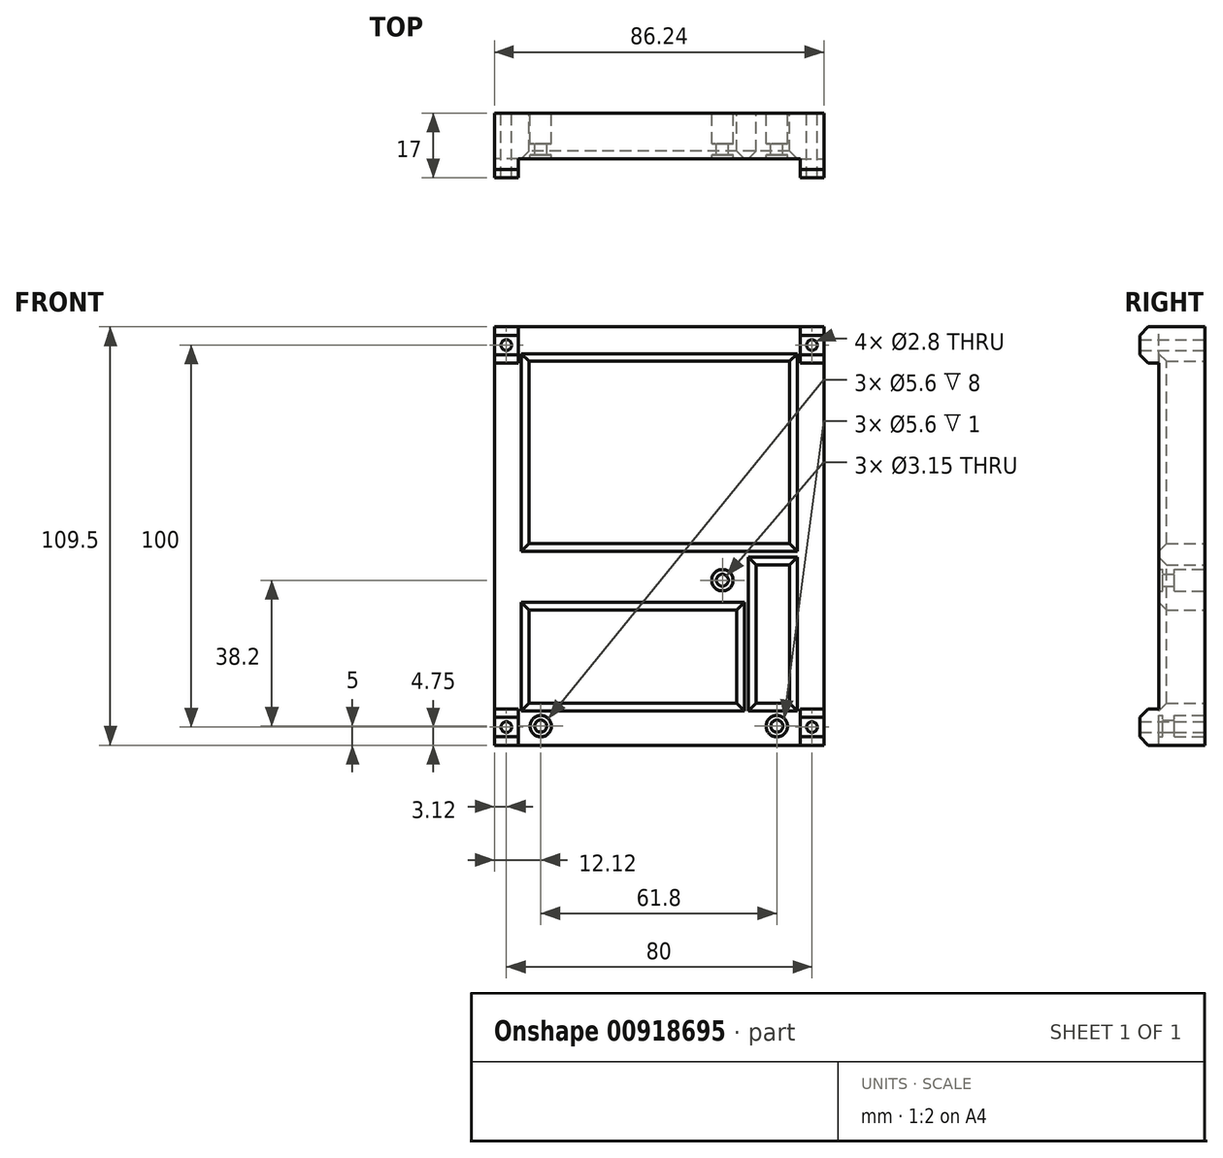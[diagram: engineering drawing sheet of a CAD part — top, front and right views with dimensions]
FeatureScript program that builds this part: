
annotation { "Feature Type Name" : "Feature", "Feature Type Description" : "" }
export const myFeature = defineFeature(function(context is Context, id is Id, definition is map)
    precondition{}
    {
        {
            var Q0;
            Q0=qCreatedBy(makeId("Front.planeOp"),FACE);
            var sketch = newSketch(context, id + "F0", { "sketchPlane" : qUnion([Q0])});
            skPoint(sketch, "E0.middle", {"position": v(0, 0) * mm});
            skCircle(sketch, "E1", {"center": v(-40, 50) * mm, "radius": 1.4 * mm});
            skCircle(sketch, "E2", {"center": v(40, 50) * mm, "radius": 1.4 * mm});
            skCircle(sketch, "E3", {"center": v(-40, -50) * mm, "radius": 1.4 * mm});
            skCircle(sketch, "E4", {"center": v(40, -50) * mm, "radius": 1.4 * mm});
            skLineSegment(sketch, "E5.bottom", {"start": v(43.12, -54.75) * mm, "end": v(-43.12, -54.75) * mm});
            skLineSegment(sketch, "E5.top", {"start": v(43.12, 54.75) * mm, "end": v(-43.12, 54.75) * mm});
            skLineSegment(sketch, "E5.left", {"start": v(43.12, -54.75) * mm, "end": v(43.12, 54.75) * mm});
            skLineSegment(sketch, "E5.right", {"start": v(-43.12, -54.75) * mm, "end": v(-43.12, 54.75) * mm});
            skLineSegment(sketch, "E6.bottom", {"start": v(-36.88, -54.75) * mm, "end": v(-43.13, -54.75) * mm});
            skLineSegment(sketch, "E6.top", {"start": v(-36.88, -45.25) * mm, "end": v(-43.13, -45.25) * mm});
            skLineSegment(sketch, "E6.left", {"start": v(-36.88, -54.75) * mm, "end": v(-36.88, -45.25) * mm});
            skLineSegment(sketch, "E6.right", {"start": v(-43.13, -54.75) * mm, "end": v(-43.13, -45.25) * mm});
            skLineSegment(sketch, "E7.bottom", {"start": v(36.88, -54.75) * mm, "end": v(43.12, -54.75) * mm});
            skLineSegment(sketch, "E7.top", {"start": v(36.88, -45.25) * mm, "end": v(43.12, -45.25) * mm});
            skLineSegment(sketch, "E7.left", {"start": v(36.88, -54.75) * mm, "end": v(36.88, -45.25) * mm});
            skLineSegment(sketch, "E7.right", {"start": v(43.12, -54.75) * mm, "end": v(43.12, -45.25) * mm});
            skLineSegment(sketch, "E8.bottom", {"start": v(-36.88, 45.25) * mm, "end": v(-43.13, 45.25) * mm});
            skLineSegment(sketch, "E8.top", {"start": v(-36.88, 54.75) * mm, "end": v(-43.13, 54.75) * mm});
            skLineSegment(sketch, "E8.left", {"start": v(-36.88, 45.25) * mm, "end": v(-36.88, 54.75) * mm});
            skLineSegment(sketch, "E8.right", {"start": v(-43.13, 45.25) * mm, "end": v(-43.13, 54.75) * mm});
            skLineSegment(sketch, "E9.bottom", {"start": v(36.88, 45.25) * mm, "end": v(43.12, 45.25) * mm});
            skLineSegment(sketch, "E9.top", {"start": v(36.87, 54.75) * mm, "end": v(43.12, 54.75) * mm});
            skLineSegment(sketch, "E9.left", {"start": v(36.88, 45.25) * mm, "end": v(36.88, 54.75) * mm});
            skLineSegment(sketch, "E9.right", {"start": v(43.12, 45.25) * mm, "end": v(43.12, 54.75) * mm});
            skCircle(sketch, "E10.cCircle", {"center": v(40, 50) * mm, "radius": 3.08 * mm, "construction": true});
            skLineSegment(sketch, "E10.0", {"start": v(36.92, 48.22) * mm, "end": v(36.92, 51.78) * mm});
            skLineSegment(sketch, "E10.1", {"start": v(36.93, 51.78) * mm, "end": v(40, 53.55) * mm});
            skLineSegment(sketch, "E10.2", {"start": v(40, 53.55) * mm, "end": v(43.07, 51.78) * mm});
            skLineSegment(sketch, "E10.3", {"start": v(43.07, 51.78) * mm, "end": v(43.08, 48.22) * mm});
            skLineSegment(sketch, "E10.4", {"start": v(43.08, 48.22) * mm, "end": v(40, 46.45) * mm});
            skLineSegment(sketch, "E10.5", {"start": v(40, 46.45) * mm, "end": v(36.93, 48.22) * mm});
            skPoint(sketch, "E10.0.midPoint", {"position": v(36.92, 50) * mm});
            skCircle(sketch, "E11.cCircle", {"center": v(-40, 50) * mm, "radius": 3.08 * mm, "construction": true});
            skLineSegment(sketch, "E11.0", {"start": v(-36.92, 51.78) * mm, "end": v(-36.92, 48.22) * mm});
            skLineSegment(sketch, "E11.1", {"start": v(-36.92, 48.22) * mm, "end": v(-40, 46.45) * mm});
            skLineSegment(sketch, "E11.2", {"start": v(-40, 46.45) * mm, "end": v(-43.07, 48.22) * mm});
            skLineSegment(sketch, "E11.3", {"start": v(-43.07, 48.22) * mm, "end": v(-43.07, 51.78) * mm});
            skLineSegment(sketch, "E11.4", {"start": v(-43.08, 51.78) * mm, "end": v(-40, 53.55) * mm});
            skLineSegment(sketch, "E11.5", {"start": v(-40, 53.55) * mm, "end": v(-36.92, 51.78) * mm});
            skPoint(sketch, "E11.0.midPoint", {"position": v(-36.92, 50) * mm});
            skCircle(sketch, "E12.cCircle", {"center": v(40, -50) * mm, "radius": 3.08 * mm, "construction": true});
            skPoint(sketch, "E12.cCircle.perimeterSnap0", {"position": v(43.12, -50) * mm});
            skLineSegment(sketch, "E12.0", {"start": v(43.08, -48.22) * mm, "end": v(43.08, -51.78) * mm});
            skLineSegment(sketch, "E12.1", {"start": v(43.07, -51.78) * mm, "end": v(40, -53.55) * mm});
            skLineSegment(sketch, "E12.2", {"start": v(40, -53.55) * mm, "end": v(36.93, -51.78) * mm});
            skLineSegment(sketch, "E12.3", {"start": v(36.93, -51.78) * mm, "end": v(36.93, -48.22) * mm});
            skLineSegment(sketch, "E12.4", {"start": v(36.93, -48.22) * mm, "end": v(40, -46.45) * mm});
            skLineSegment(sketch, "E12.5", {"start": v(40, -46.45) * mm, "end": v(43.07, -48.22) * mm});
            skPoint(sketch, "E12.0.midPoint", {"position": v(43.08, -50) * mm});
            skPoint(sketch, "E12.0.midPoint.positionSnap0", {"position": v(43.12, -50) * mm});
            skCircle(sketch, "E13.cCircle", {"center": v(-40, -50) * mm, "radius": 3.08 * mm, "construction": true});
            skLineSegment(sketch, "E13.0", {"start": v(-36.93, -48.22) * mm, "end": v(-36.93, -51.78) * mm});
            skLineSegment(sketch, "E13.1", {"start": v(-36.93, -51.78) * mm, "end": v(-40, -53.55) * mm});
            skLineSegment(sketch, "E13.2", {"start": v(-40, -53.55) * mm, "end": v(-43.08, -51.78) * mm});
            skLineSegment(sketch, "E13.3", {"start": v(-43.08, -51.78) * mm, "end": v(-43.08, -48.22) * mm});
            skLineSegment(sketch, "E13.4", {"start": v(-43.08, -48.22) * mm, "end": v(-40, -46.45) * mm});
            skLineSegment(sketch, "E13.5", {"start": v(-40, -46.45) * mm, "end": v(-36.93, -48.22) * mm});
            skPoint(sketch, "E13.0.midPoint", {"position": v(-36.93, -50) * mm});
            skCircle(sketch, "E14", {"center": v(-31, -49.75) * mm, "radius": 1.57 * mm});
            skCircle(sketch, "E15", {"center": v(30.8, -49.75) * mm, "radius": 1.57 * mm});
            skCircle(sketch, "E16", {"center": v(-31, -49.75) * mm, "radius": 2.8 * mm});
            skCircle(sketch, "E17", {"center": v(30.8, -49.75) * mm, "radius": 2.8 * mm});
            skCircle(sketch, "E18", {"center": v(16.55, -11.55) * mm, "radius": 2.8 * mm});
            skCircle(sketch, "E19", {"center": v(16.55, -11.55) * mm, "radius": 1.57 * mm});
            skLineSegment(sketch, "E20", {"start": v(-31, -49.75) * mm, "end": v(30.8, -49.75) * mm, "construction": true});
            skLineSegment(sketch, "E21", {"start": v(16.55, -11.55) * mm, "end": v(16.55, -49.75) * mm, "construction": true});
            skSolve(sketch);
        }
        {
            var Q0;
            {var subQ3=sQuery(id+"F0.wireOp",EDGE,"E6.top");Q0=makeQuery(id+"F0.imprint","IMPRINT",FACE,{"disambiguationData":[TD([[makeQuery(id+"F0.imprint","IMPRINT",EDGE,{"derivedFrom":subQ3}),-1.0]])]});}
            var Q1;
            {var subQ0=sQuery(id+"F0.wireOp",EDGE,"LAEbAKdu-djDs-V827-S9WD-6yGzL6sm2GWT");Q1=makeQuery(id+"F0.imprint","IMPRINT",FACE,{"disambiguationData":[TD([[makeQuery(id+"F0.imprint","IMPRINT",EDGE,{"derivedFrom":subQ0}),1.0]])]});}
            var Q2;
            Q2=makeQuery(id+"F0.imprint","IMPRINT",FACE,{"disambiguationData":[TD([[makeQuery(id+"F0.imprint","IMPRINT",EDGE,{"derivedFrom":sQuery(id+"F0.wireOp",EDGE,"344f14d0-57c9-4bf9-bac3-c7a6806c6285.bottom")}),-1.0]])]});
            var Q3;
            Q3=makeQuery(id+"F0.imprint","IMPRINT",FACE,{"disambiguationData":[TD([[makeQuery(id+"F0.imprint","IMPRINT",EDGE,{"derivedFrom":sQuery(id+"F0.wireOp",EDGE,"9oMv4eh1-cItz-VmmB-YfER-I7rwddDMCMIy.bottom")}),-1.0]])]});
            var Q4;
            Q4=makeQuery(id+"F0.imprint","IMPRINT",FACE,{"disambiguationData":[TD([[makeQuery(id+"F0.imprint","IMPRINT",EDGE,{"derivedFrom":sQuery(id+"F0.wireOp",EDGE,"1293f738-cd9c-4ca6-888c-53c8c5076d64.bottom")}),-1.0]])]});
            var Q5;
            Q5=makeQuery(id+"F0.imprint","IMPRINT",FACE,{"disambiguationData":[TD([[makeQuery(id+"F0.imprint","IMPRINT",EDGE,{"derivedFrom":sQuery(id+"F0.wireOp",EDGE,"8f083a88-c7b4-469a-ac29-3101791f455f.bottom")}),-1.0]])]});
            var Q6;
            Q6=makeQuery(id+"F0.imprint","IMPRINT",FACE,{"disambiguationData":[TD([[makeQuery(id+"F0.imprint","IMPRINT",EDGE,{"derivedFrom":sQuery(id+"F0.wireOp",EDGE,"92fa807a-3ddb-4387-94e5-abf9c8788f89.bottom")}),-1.0]])]});
            var Q7;
            Q7=makeQuery(id+"F0.imprint","IMPRINT",FACE,{"disambiguationData":[TD([[makeQuery(id+"F0.imprint","IMPRINT",EDGE,{"derivedFrom":sQuery(id+"F0.wireOp",EDGE,"303d7d46-c817-43ee-aa70-cb5fa533f4f4.bottom")}),-1.0]])]});
            extrude(context, id + "F1", {"entities" : qUnion([Q0, Q1, Q2, Q3, Q4, Q5, Q6, Q7]), "depth" : 12 * mm, "offsetDistance" : 25 * mm});
        }
        {
            var Q0;
            Q0=makeQuery(id+"F0.imprint","IMPRINT",FACE,{"disambiguationData":[TD([[makeQuery(id+"F0.imprint","IMPRINT",EDGE,{"derivedFrom":sQuery(id+"F0.wireOp",EDGE,"E3")}),-1.0]])]});
            var Q1;
            Q1=makeQuery(id+"F0.imprint","IMPRINT",FACE,{"disambiguationData":[TD([[makeQuery(id+"F0.imprint","IMPRINT",EDGE,{"derivedFrom":sQuery(id+"F0.wireOp",EDGE,"E4")}),-1.0]])]});
            var Q2;
            Q2=makeQuery(id+"F0.imprint","IMPRINT",FACE,{"disambiguationData":[TD([[makeQuery(id+"F0.imprint","IMPRINT",EDGE,{"derivedFrom":sQuery(id+"F0.wireOp",EDGE,"E2")}),-1.0]])]});
            var Q3;
            Q3=makeQuery(id+"F0.imprint","IMPRINT",FACE,{"disambiguationData":[TD([[makeQuery(id+"F0.imprint","IMPRINT",EDGE,{"derivedFrom":sQuery(id+"F0.wireOp",EDGE,"E1")}),-1.0]])]});
            var Q4;
            {var subQ1=sQuery(id+"F0.wireOp",EDGE,"E7.top");Q4=makeQuery(id+"F0.imprint","IMPRINT",FACE,{"disambiguationData":[TD([[makeQuery(id+"F0.imprint","IMPRINT",EDGE,{"derivedFrom":subQ1}),-1.0]])]});}
            var Q5;
            {var subQ1=sQuery(id+"F0.wireOp",EDGE,"E6.top");Q5=makeQuery(id+"F0.imprint","IMPRINT",FACE,{"disambiguationData":[TD([[makeQuery(id+"F0.imprint","IMPRINT",EDGE,{"derivedFrom":subQ1}),1.0]])]});}
            var Q6;
            {var subQ1=sQuery(id+"F0.wireOp",EDGE,"E8.bottom");Q6=makeQuery(id+"F0.imprint","IMPRINT",FACE,{"disambiguationData":[TD([[makeQuery(id+"F0.imprint","IMPRINT",EDGE,{"derivedFrom":subQ1}),-1.0]])]});}
            var Q7;
            {var subQ0=sQuery(id+"F0.wireOp",EDGE,"E9.bottom");Q7=makeQuery(id+"F0.imprint","IMPRINT",FACE,{"disambiguationData":[TD([[makeQuery(id+"F0.imprint","IMPRINT",EDGE,{"derivedFrom":subQ0}),1.0]])]});}
            extrude(context, id + "F2", {"entities" : qUnion([Q0, Q1, Q2, Q3, Q4, Q5, Q6, Q7]), "operationType" : NewBodyOperationType.ADD, "depth" : 17 * mm, "offsetDistance" : 25 * mm});
        }
        {
            var Q0;
            Q0=makeQuery(id+"F2.opExtrude","CAP_EDGE",EDGE,{"disambiguationData":[OSD([sQuery(id+"F0.wireOp",EDGE,"E6.top")])],"isStart":false});
            var Q1;
            {var subQ0=sQuery(id+"F0.wireOp",EDGE,"E5.bottom");Q1=makeQuery(id+"F2.opExtrude","CAP_EDGE",EDGE,{"disambiguationData":[OSD([subQ0]),TDD([makeQuery(id+"F0.imprint","IMPRINT",EDGE,{"disambiguationData":[TD([[makeQuery(id+"F0.imprint","INTERSECT",VERTEX,{"derivedFrom":[subQ0,sQuery(id+"F0.wireOp",EDGE,"E6.left")]}),-1.0]])],"derivedFrom":subQ0})])],"isStart":false});}
            var Q2;
            Q2=makeQuery(id+"F2.opExtrude","CAP_EDGE",EDGE,{"disambiguationData":[OSD([sQuery(id+"F0.wireOp",EDGE,"E7.top")])],"isStart":false});
            var Q3;
            {var subQ0=sQuery(id+"F0.wireOp",EDGE,"E5.bottom");Q3=makeQuery(id+"F2.opExtrude","CAP_EDGE",EDGE,{"disambiguationData":[OSD([subQ0]),TDD([makeQuery(id+"F0.imprint","IMPRINT",EDGE,{"disambiguationData":[TD([[makeQuery(id+"F0.imprint","INTERSECT",VERTEX,{"derivedFrom":[subQ0,sQuery(id+"F0.wireOp",EDGE,"E7.left")]}),1.0]])],"derivedFrom":subQ0})])],"isStart":false});}
            var Q4;
            {var subQ0=sQuery(id+"F0.wireOp",EDGE,"E5.top");Q4=makeQuery(id+"F2.opExtrude","CAP_EDGE",EDGE,{"disambiguationData":[OSD([subQ0]),TDD([makeQuery(id+"F0.imprint","IMPRINT",EDGE,{"disambiguationData":[TD([[makeQuery(id+"F0.imprint","INTERSECT",VERTEX,{"derivedFrom":[subQ0,sQuery(id+"F0.wireOp",EDGE,"E5.right")]}),1.0]])],"derivedFrom":subQ0})])],"isStart":false});}
            var Q5;
            Q5=makeQuery(id+"F2.opExtrude","CAP_EDGE",EDGE,{"disambiguationData":[OSD([sQuery(id+"F0.wireOp",EDGE,"E8.bottom")])],"isStart":false});
            var Q6;
            {var subQ0=sQuery(id+"F0.wireOp",EDGE,"E5.top");Q6=makeQuery(id+"F2.opExtrude","CAP_EDGE",EDGE,{"disambiguationData":[OSD([subQ0]),TDD([makeQuery(id+"F0.imprint","IMPRINT",EDGE,{"disambiguationData":[TD([[makeQuery(id+"F0.imprint","INTERSECT",VERTEX,{"derivedFrom":[subQ0,sQuery(id+"F0.wireOp",EDGE,"E9.left")]}),1.0]])],"derivedFrom":subQ0})])],"isStart":false});}
            var Q7;
            Q7=makeQuery(id+"F2.opExtrude","CAP_EDGE",EDGE,{"disambiguationData":[OSD([sQuery(id+"F0.wireOp",EDGE,"E9.bottom")])],"isStart":false});
            chamfer(context, id + "F3", {"entities" : qUnion([Q0, Q1, Q2, Q3, Q4, Q5, Q6, Q7]), "width" : 2.2 * mm, "tangentPropagation" : true});
        }
        {
            var Q0;
            Q0=makeQuery(id+"F0.imprint","IMPRINT",FACE,{"disambiguationData":[TD([[makeQuery(id+"F0.imprint","IMPRINT",EDGE,{"derivedFrom":sQuery(id+"F0.wireOp",EDGE,"E18")}),1.0]])]});
            var Q1;
            Q1=makeQuery(id+"F0.imprint","IMPRINT",FACE,{"disambiguationData":[TD([[makeQuery(id+"F0.imprint","IMPRINT",EDGE,{"derivedFrom":sQuery(id+"F0.wireOp",EDGE,"E15")}),-1.0]])]});
            var Q2;
            Q2=makeQuery(id+"F0.imprint","IMPRINT",FACE,{"disambiguationData":[TD([[makeQuery(id+"F0.imprint","IMPRINT",EDGE,{"derivedFrom":sQuery(id+"F0.wireOp",EDGE,"E14")}),-1.0]])]});
            extrude(context, id + "F4", {"entities" : qUnion([Q0, Q1, Q2]), "operationType" : NewBodyOperationType.ADD, "depth" : 11 * mm, "offsetDistance" : 25 * mm, "hasSecondDirection" : true, "secondDirectionOppositeDirection" : true, "secondDirectionDepth" : -8 * mm});
        }
        {
            var Q0;
            {var subQ0=sQuery(id+"F0.wireOp",EDGE,"E7.left");var subQ1=sQuery(id+"F0.wireOp",EDGE,"E7.top");var subQ2=sQuery(id+"F0.wireOp",EDGE,"E5.left");var subQ3=sQuery(id+"F0.wireOp",EDGE,"E5.bottom");var subQ4=sQuery(id+"F0.wireOp",EDGE,"E6.left");var subQ5=sQuery(id+"F0.wireOp",EDGE,"E6.top");var subQ6=sQuery(id+"F0.wireOp",EDGE,"E5.right");var subQ7=sQuery(id+"F0.wireOp",EDGE,"E9.left");var subQ8=sQuery(id+"F0.wireOp",EDGE,"E9.bottom");var subQ9=sQuery(id+"F0.wireOp",EDGE,"E5.top");var subQ10=sQuery(id+"F0.wireOp",EDGE,"E8.left");var subQ11=sQuery(id+"F0.wireOp",EDGE,"E8.bottom");Q0=makeQuery(id+"F2.boolean.opBoolean","MERGE",FACE,{"derivedFrom":[makeQuery(id+"F1.opExtrude","CAP_FACE",FACE,{"disambiguationData":[OSD([subQ3,subQ9,subQ2,subQ6,subQ5,subQ4,subQ1,subQ0,subQ11,subQ10,subQ8,subQ7,sQuery(id+"F0.wireOp",EDGE,"E16"),sQuery(id+"F0.wireOp",EDGE,"E17"),sQuery(id+"F0.wireOp",EDGE,"E18")])],"isStart":true}),makeQuery(id+"F2.opExtrude","CAP_FACE",FACE,{"disambiguationData":[OSD([sQuery(id+"F0.wireOp",EDGE,"E1"),subQ9,subQ6,subQ11,subQ10])],"isStart":true}),makeQuery(id+"F2.opExtrude","CAP_FACE",FACE,{"disambiguationData":[OSD([sQuery(id+"F0.wireOp",EDGE,"E2"),subQ9,subQ2,subQ8,subQ7])],"isStart":true}),makeQuery(id+"F2.opExtrude","CAP_FACE",FACE,{"disambiguationData":[OSD([sQuery(id+"F0.wireOp",EDGE,"E3"),subQ3,subQ6,subQ5,subQ4])],"isStart":true}),makeQuery(id+"F2.opExtrude","CAP_FACE",FACE,{"disambiguationData":[OSD([sQuery(id+"F0.wireOp",EDGE,"E4"),subQ3,subQ2,subQ1,subQ0])],"isStart":true})]});}
            var sketch = newSketch(context, id + "F5", { "sketchPlane" : qUnion([Q0])});
            skLineSegment(sketch, "E22.bottom", {"start": v(-34.12, 45.75) * mm, "end": v(34.12, 45.75) * mm});
            skLineSegment(sketch, "E22.top", {"start": v(-34.12, -2) * mm, "end": v(34.12, -2) * mm});
            skLineSegment(sketch, "E22.left", {"start": v(-34.12, 45.75) * mm, "end": v(-34.12, -2) * mm});
            skLineSegment(sketch, "E22.right", {"start": v(34.12, 45.75) * mm, "end": v(34.12, -2) * mm});
            skLineSegment(sketch, "E23.bottom", {"start": v(-34.12, -7.52) * mm, "end": v(-25.35, -7.52) * mm});
            skLineSegment(sketch, "E23.top", {"start": v(-34.12, -43.75) * mm, "end": v(-25.35, -43.75) * mm});
            skLineSegment(sketch, "E23.left", {"start": v(-34.12, -7.52) * mm, "end": v(-34.12, -43.75) * mm});
            skLineSegment(sketch, "E23.right", {"start": v(-25.35, -7.52) * mm, "end": v(-25.35, -43.75) * mm});
            skLineSegment(sketch, "E24.bottom", {"start": v(-20.35, -19.35) * mm, "end": v(34.12, -19.35) * mm});
            skLineSegment(sketch, "E24.top", {"start": v(-20.35, -43.75) * mm, "end": v(34.12, -43.75) * mm});
            skLineSegment(sketch, "E24.left", {"start": v(-20.35, -19.35) * mm, "end": v(-20.35, -43.75) * mm});
            skLineSegment(sketch, "E24.right", {"start": v(34.12, -19.35) * mm, "end": v(34.12, -43.75) * mm});
            skSolve(sketch);
        }
        {
            var Q0;
            Q0=makeQuery(id+"F5.imprint","IMPRINT",FACE,{"disambiguationData":[TD([[makeQuery(id+"F5.imprint","IMPRINT",EDGE,{"derivedFrom":sQuery(id+"F5.wireOp",EDGE,"E22.bottom")}),-1.0]])]});
            var Q1;
            Q1=makeQuery(id+"F5.imprint","IMPRINT",FACE,{"disambiguationData":[TD([[makeQuery(id+"F5.imprint","IMPRINT",EDGE,{"derivedFrom":sQuery(id+"F5.wireOp",EDGE,"E23.bottom")}),-1.0]])]});
            var Q2;
            Q2=makeQuery(id+"F5.imprint","IMPRINT",FACE,{"disambiguationData":[TD([[makeQuery(id+"F5.imprint","IMPRINT",EDGE,{"derivedFrom":sQuery(id+"F5.wireOp",EDGE,"E24.bottom")}),-1.0]])]});
            extrude(context, id + "F6", {"entities" : qUnion([Q0, Q1, Q2]), "operationType" : NewBodyOperationType.REMOVE, "oppositeDirection" : true, "depth" : 28 * mm, "offsetDistance" : 25 * mm});
        }
        {
            var Q0;
            Q0=makeQuery(id+"F6.boolean.opBoolean","INTERSECT",EDGE,{"derivedFrom":[makeQuery(id+"F1.opExtrude","CAP_FACE",FACE,{"disambiguationData":[OSD([sQuery(id+"F0.wireOp",EDGE,"E5.bottom"),sQuery(id+"F0.wireOp",EDGE,"E5.top"),sQuery(id+"F0.wireOp",EDGE,"E5.left"),sQuery(id+"F0.wireOp",EDGE,"E5.right"),sQuery(id+"F0.wireOp",EDGE,"E6.top"),sQuery(id+"F0.wireOp",EDGE,"E6.left"),sQuery(id+"F0.wireOp",EDGE,"E7.top"),sQuery(id+"F0.wireOp",EDGE,"E7.left"),sQuery(id+"F0.wireOp",EDGE,"E8.bottom"),sQuery(id+"F0.wireOp",EDGE,"E8.left"),sQuery(id+"F0.wireOp",EDGE,"E9.bottom"),sQuery(id+"F0.wireOp",EDGE,"E9.left"),sQuery(id+"F0.wireOp",EDGE,"E16"),sQuery(id+"F0.wireOp",EDGE,"E17"),sQuery(id+"F0.wireOp",EDGE,"E18")])],"isStart":false}),makeQuery(id+"F6.opExtrude","SWEPT_FACE",FACE,{"disambiguationData":[OSD([sQuery(id+"F5.wireOp",EDGE,"E22.top")])]})]});
            var Q1;
            Q1=makeQuery(id+"F6.boolean.opBoolean","INTERSECT",EDGE,{"derivedFrom":[makeQuery(id+"F1.opExtrude","CAP_FACE",FACE,{"disambiguationData":[OSD([sQuery(id+"F0.wireOp",EDGE,"E5.bottom"),sQuery(id+"F0.wireOp",EDGE,"E5.top"),sQuery(id+"F0.wireOp",EDGE,"E5.left"),sQuery(id+"F0.wireOp",EDGE,"E5.right"),sQuery(id+"F0.wireOp",EDGE,"E6.top"),sQuery(id+"F0.wireOp",EDGE,"E6.left"),sQuery(id+"F0.wireOp",EDGE,"E7.top"),sQuery(id+"F0.wireOp",EDGE,"E7.left"),sQuery(id+"F0.wireOp",EDGE,"E8.bottom"),sQuery(id+"F0.wireOp",EDGE,"E8.left"),sQuery(id+"F0.wireOp",EDGE,"E9.bottom"),sQuery(id+"F0.wireOp",EDGE,"E9.left"),sQuery(id+"F0.wireOp",EDGE,"E16"),sQuery(id+"F0.wireOp",EDGE,"E17"),sQuery(id+"F0.wireOp",EDGE,"E18")])],"isStart":false}),makeQuery(id+"F6.opExtrude","SWEPT_FACE",FACE,{"disambiguationData":[OSD([sQuery(id+"F5.wireOp",EDGE,"E22.right")])]})]});
            var Q2;
            Q2=makeQuery(id+"F6.boolean.opBoolean","INTERSECT",EDGE,{"derivedFrom":[makeQuery(id+"F1.opExtrude","CAP_FACE",FACE,{"disambiguationData":[OSD([sQuery(id+"F0.wireOp",EDGE,"E5.bottom"),sQuery(id+"F0.wireOp",EDGE,"E5.top"),sQuery(id+"F0.wireOp",EDGE,"E5.left"),sQuery(id+"F0.wireOp",EDGE,"E5.right"),sQuery(id+"F0.wireOp",EDGE,"E6.top"),sQuery(id+"F0.wireOp",EDGE,"E6.left"),sQuery(id+"F0.wireOp",EDGE,"E7.top"),sQuery(id+"F0.wireOp",EDGE,"E7.left"),sQuery(id+"F0.wireOp",EDGE,"E8.bottom"),sQuery(id+"F0.wireOp",EDGE,"E8.left"),sQuery(id+"F0.wireOp",EDGE,"E9.bottom"),sQuery(id+"F0.wireOp",EDGE,"E9.left"),sQuery(id+"F0.wireOp",EDGE,"E16"),sQuery(id+"F0.wireOp",EDGE,"E17"),sQuery(id+"F0.wireOp",EDGE,"E18")])],"isStart":false}),makeQuery(id+"F6.opExtrude","SWEPT_FACE",FACE,{"disambiguationData":[OSD([sQuery(id+"F5.wireOp",EDGE,"E22.bottom")])]})]});
            var Q3;
            Q3=makeQuery(id+"F6.boolean.opBoolean","INTERSECT",EDGE,{"derivedFrom":[makeQuery(id+"F1.opExtrude","CAP_FACE",FACE,{"disambiguationData":[OSD([sQuery(id+"F0.wireOp",EDGE,"E5.bottom"),sQuery(id+"F0.wireOp",EDGE,"E5.top"),sQuery(id+"F0.wireOp",EDGE,"E5.left"),sQuery(id+"F0.wireOp",EDGE,"E5.right"),sQuery(id+"F0.wireOp",EDGE,"E6.top"),sQuery(id+"F0.wireOp",EDGE,"E6.left"),sQuery(id+"F0.wireOp",EDGE,"E7.top"),sQuery(id+"F0.wireOp",EDGE,"E7.left"),sQuery(id+"F0.wireOp",EDGE,"E8.bottom"),sQuery(id+"F0.wireOp",EDGE,"E8.left"),sQuery(id+"F0.wireOp",EDGE,"E9.bottom"),sQuery(id+"F0.wireOp",EDGE,"E9.left"),sQuery(id+"F0.wireOp",EDGE,"E16"),sQuery(id+"F0.wireOp",EDGE,"E17"),sQuery(id+"F0.wireOp",EDGE,"E18")])],"isStart":false}),makeQuery(id+"F6.opExtrude","SWEPT_FACE",FACE,{"disambiguationData":[OSD([sQuery(id+"F5.wireOp",EDGE,"E22.left")])]})]});
            var Q4;
            Q4=makeQuery(id+"F6.boolean.opBoolean","INTERSECT",EDGE,{"derivedFrom":[makeQuery(id+"F1.opExtrude","CAP_FACE",FACE,{"disambiguationData":[OSD([sQuery(id+"F0.wireOp",EDGE,"E5.bottom"),sQuery(id+"F0.wireOp",EDGE,"E5.top"),sQuery(id+"F0.wireOp",EDGE,"E5.left"),sQuery(id+"F0.wireOp",EDGE,"E5.right"),sQuery(id+"F0.wireOp",EDGE,"E6.top"),sQuery(id+"F0.wireOp",EDGE,"E6.left"),sQuery(id+"F0.wireOp",EDGE,"E7.top"),sQuery(id+"F0.wireOp",EDGE,"E7.left"),sQuery(id+"F0.wireOp",EDGE,"E8.bottom"),sQuery(id+"F0.wireOp",EDGE,"E8.left"),sQuery(id+"F0.wireOp",EDGE,"E9.bottom"),sQuery(id+"F0.wireOp",EDGE,"E9.left"),sQuery(id+"F0.wireOp",EDGE,"E16"),sQuery(id+"F0.wireOp",EDGE,"E17"),sQuery(id+"F0.wireOp",EDGE,"E18")])],"isStart":false}),makeQuery(id+"F6.opExtrude","SWEPT_FACE",FACE,{"disambiguationData":[OSD([sQuery(id+"F5.wireOp",EDGE,"E23.left")])]})]});
            var Q5;
            Q5=makeQuery(id+"F6.boolean.opBoolean","INTERSECT",EDGE,{"derivedFrom":[makeQuery(id+"F1.opExtrude","CAP_FACE",FACE,{"disambiguationData":[OSD([sQuery(id+"F0.wireOp",EDGE,"E5.bottom"),sQuery(id+"F0.wireOp",EDGE,"E5.top"),sQuery(id+"F0.wireOp",EDGE,"E5.left"),sQuery(id+"F0.wireOp",EDGE,"E5.right"),sQuery(id+"F0.wireOp",EDGE,"E6.top"),sQuery(id+"F0.wireOp",EDGE,"E6.left"),sQuery(id+"F0.wireOp",EDGE,"E7.top"),sQuery(id+"F0.wireOp",EDGE,"E7.left"),sQuery(id+"F0.wireOp",EDGE,"E8.bottom"),sQuery(id+"F0.wireOp",EDGE,"E8.left"),sQuery(id+"F0.wireOp",EDGE,"E9.bottom"),sQuery(id+"F0.wireOp",EDGE,"E9.left"),sQuery(id+"F0.wireOp",EDGE,"E16"),sQuery(id+"F0.wireOp",EDGE,"E17"),sQuery(id+"F0.wireOp",EDGE,"E18")])],"isStart":false}),makeQuery(id+"F6.opExtrude","SWEPT_FACE",FACE,{"disambiguationData":[OSD([sQuery(id+"F5.wireOp",EDGE,"E23.bottom")])]})]});
            var Q6;
            Q6=makeQuery(id+"F6.boolean.opBoolean","INTERSECT",EDGE,{"derivedFrom":[makeQuery(id+"F1.opExtrude","CAP_FACE",FACE,{"disambiguationData":[OSD([sQuery(id+"F0.wireOp",EDGE,"E5.bottom"),sQuery(id+"F0.wireOp",EDGE,"E5.top"),sQuery(id+"F0.wireOp",EDGE,"E5.left"),sQuery(id+"F0.wireOp",EDGE,"E5.right"),sQuery(id+"F0.wireOp",EDGE,"E6.top"),sQuery(id+"F0.wireOp",EDGE,"E6.left"),sQuery(id+"F0.wireOp",EDGE,"E7.top"),sQuery(id+"F0.wireOp",EDGE,"E7.left"),sQuery(id+"F0.wireOp",EDGE,"E8.bottom"),sQuery(id+"F0.wireOp",EDGE,"E8.left"),sQuery(id+"F0.wireOp",EDGE,"E9.bottom"),sQuery(id+"F0.wireOp",EDGE,"E9.left"),sQuery(id+"F0.wireOp",EDGE,"E16"),sQuery(id+"F0.wireOp",EDGE,"E17"),sQuery(id+"F0.wireOp",EDGE,"E18")])],"isStart":false}),makeQuery(id+"F6.opExtrude","SWEPT_FACE",FACE,{"disambiguationData":[OSD([sQuery(id+"F5.wireOp",EDGE,"E23.right")])]})]});
            var Q7;
            Q7=makeQuery(id+"F6.boolean.opBoolean","INTERSECT",EDGE,{"derivedFrom":[makeQuery(id+"F1.opExtrude","CAP_FACE",FACE,{"disambiguationData":[OSD([sQuery(id+"F0.wireOp",EDGE,"E5.bottom"),sQuery(id+"F0.wireOp",EDGE,"E5.top"),sQuery(id+"F0.wireOp",EDGE,"E5.left"),sQuery(id+"F0.wireOp",EDGE,"E5.right"),sQuery(id+"F0.wireOp",EDGE,"E6.top"),sQuery(id+"F0.wireOp",EDGE,"E6.left"),sQuery(id+"F0.wireOp",EDGE,"E7.top"),sQuery(id+"F0.wireOp",EDGE,"E7.left"),sQuery(id+"F0.wireOp",EDGE,"E8.bottom"),sQuery(id+"F0.wireOp",EDGE,"E8.left"),sQuery(id+"F0.wireOp",EDGE,"E9.bottom"),sQuery(id+"F0.wireOp",EDGE,"E9.left"),sQuery(id+"F0.wireOp",EDGE,"E16"),sQuery(id+"F0.wireOp",EDGE,"E17"),sQuery(id+"F0.wireOp",EDGE,"E18")])],"isStart":false}),makeQuery(id+"F6.opExtrude","SWEPT_FACE",FACE,{"disambiguationData":[OSD([sQuery(id+"F5.wireOp",EDGE,"E23.top")])]})]});
            var Q8;
            Q8=makeQuery(id+"F6.boolean.opBoolean","INTERSECT",EDGE,{"derivedFrom":[makeQuery(id+"F1.opExtrude","CAP_FACE",FACE,{"disambiguationData":[OSD([sQuery(id+"F0.wireOp",EDGE,"E5.bottom"),sQuery(id+"F0.wireOp",EDGE,"E5.top"),sQuery(id+"F0.wireOp",EDGE,"E5.left"),sQuery(id+"F0.wireOp",EDGE,"E5.right"),sQuery(id+"F0.wireOp",EDGE,"E6.top"),sQuery(id+"F0.wireOp",EDGE,"E6.left"),sQuery(id+"F0.wireOp",EDGE,"E7.top"),sQuery(id+"F0.wireOp",EDGE,"E7.left"),sQuery(id+"F0.wireOp",EDGE,"E8.bottom"),sQuery(id+"F0.wireOp",EDGE,"E8.left"),sQuery(id+"F0.wireOp",EDGE,"E9.bottom"),sQuery(id+"F0.wireOp",EDGE,"E9.left"),sQuery(id+"F0.wireOp",EDGE,"E16"),sQuery(id+"F0.wireOp",EDGE,"E17"),sQuery(id+"F0.wireOp",EDGE,"E18")])],"isStart":false}),makeQuery(id+"F6.opExtrude","SWEPT_FACE",FACE,{"disambiguationData":[OSD([sQuery(id+"F5.wireOp",EDGE,"E24.top")])]})]});
            var Q9;
            Q9=makeQuery(id+"F6.boolean.opBoolean","INTERSECT",EDGE,{"derivedFrom":[makeQuery(id+"F1.opExtrude","CAP_FACE",FACE,{"disambiguationData":[OSD([sQuery(id+"F0.wireOp",EDGE,"E5.bottom"),sQuery(id+"F0.wireOp",EDGE,"E5.top"),sQuery(id+"F0.wireOp",EDGE,"E5.left"),sQuery(id+"F0.wireOp",EDGE,"E5.right"),sQuery(id+"F0.wireOp",EDGE,"E6.top"),sQuery(id+"F0.wireOp",EDGE,"E6.left"),sQuery(id+"F0.wireOp",EDGE,"E7.top"),sQuery(id+"F0.wireOp",EDGE,"E7.left"),sQuery(id+"F0.wireOp",EDGE,"E8.bottom"),sQuery(id+"F0.wireOp",EDGE,"E8.left"),sQuery(id+"F0.wireOp",EDGE,"E9.bottom"),sQuery(id+"F0.wireOp",EDGE,"E9.left"),sQuery(id+"F0.wireOp",EDGE,"E16"),sQuery(id+"F0.wireOp",EDGE,"E17"),sQuery(id+"F0.wireOp",EDGE,"E18")])],"isStart":false}),makeQuery(id+"F6.opExtrude","SWEPT_FACE",FACE,{"disambiguationData":[OSD([sQuery(id+"F5.wireOp",EDGE,"E24.left")])]})]});
            var Q10;
            Q10=makeQuery(id+"F6.boolean.opBoolean","INTERSECT",EDGE,{"derivedFrom":[makeQuery(id+"F1.opExtrude","CAP_FACE",FACE,{"disambiguationData":[OSD([sQuery(id+"F0.wireOp",EDGE,"E5.bottom"),sQuery(id+"F0.wireOp",EDGE,"E5.top"),sQuery(id+"F0.wireOp",EDGE,"E5.left"),sQuery(id+"F0.wireOp",EDGE,"E5.right"),sQuery(id+"F0.wireOp",EDGE,"E6.top"),sQuery(id+"F0.wireOp",EDGE,"E6.left"),sQuery(id+"F0.wireOp",EDGE,"E7.top"),sQuery(id+"F0.wireOp",EDGE,"E7.left"),sQuery(id+"F0.wireOp",EDGE,"E8.bottom"),sQuery(id+"F0.wireOp",EDGE,"E8.left"),sQuery(id+"F0.wireOp",EDGE,"E9.bottom"),sQuery(id+"F0.wireOp",EDGE,"E9.left"),sQuery(id+"F0.wireOp",EDGE,"E16"),sQuery(id+"F0.wireOp",EDGE,"E17"),sQuery(id+"F0.wireOp",EDGE,"E18")])],"isStart":false}),makeQuery(id+"F6.opExtrude","SWEPT_FACE",FACE,{"disambiguationData":[OSD([sQuery(id+"F5.wireOp",EDGE,"E24.bottom")])]})]});
            var Q11;
            Q11=makeQuery(id+"F6.boolean.opBoolean","INTERSECT",EDGE,{"derivedFrom":[makeQuery(id+"F1.opExtrude","CAP_FACE",FACE,{"disambiguationData":[OSD([sQuery(id+"F0.wireOp",EDGE,"E5.bottom"),sQuery(id+"F0.wireOp",EDGE,"E5.top"),sQuery(id+"F0.wireOp",EDGE,"E5.left"),sQuery(id+"F0.wireOp",EDGE,"E5.right"),sQuery(id+"F0.wireOp",EDGE,"E6.top"),sQuery(id+"F0.wireOp",EDGE,"E6.left"),sQuery(id+"F0.wireOp",EDGE,"E7.top"),sQuery(id+"F0.wireOp",EDGE,"E7.left"),sQuery(id+"F0.wireOp",EDGE,"E8.bottom"),sQuery(id+"F0.wireOp",EDGE,"E8.left"),sQuery(id+"F0.wireOp",EDGE,"E9.bottom"),sQuery(id+"F0.wireOp",EDGE,"E9.left"),sQuery(id+"F0.wireOp",EDGE,"E16"),sQuery(id+"F0.wireOp",EDGE,"E17"),sQuery(id+"F0.wireOp",EDGE,"E18")])],"isStart":false}),makeQuery(id+"F6.opExtrude","SWEPT_FACE",FACE,{"disambiguationData":[OSD([sQuery(id+"F5.wireOp",EDGE,"E24.right")])]})]});
            chamfer(context, id + "F7", {"entities" : qUnion([Q0, Q1, Q2, Q3, Q4, Q5, Q6, Q7, Q8, Q9, Q10, Q11]), "width" : 2 * mm, "tangentPropagation" : true});
        }
    });
